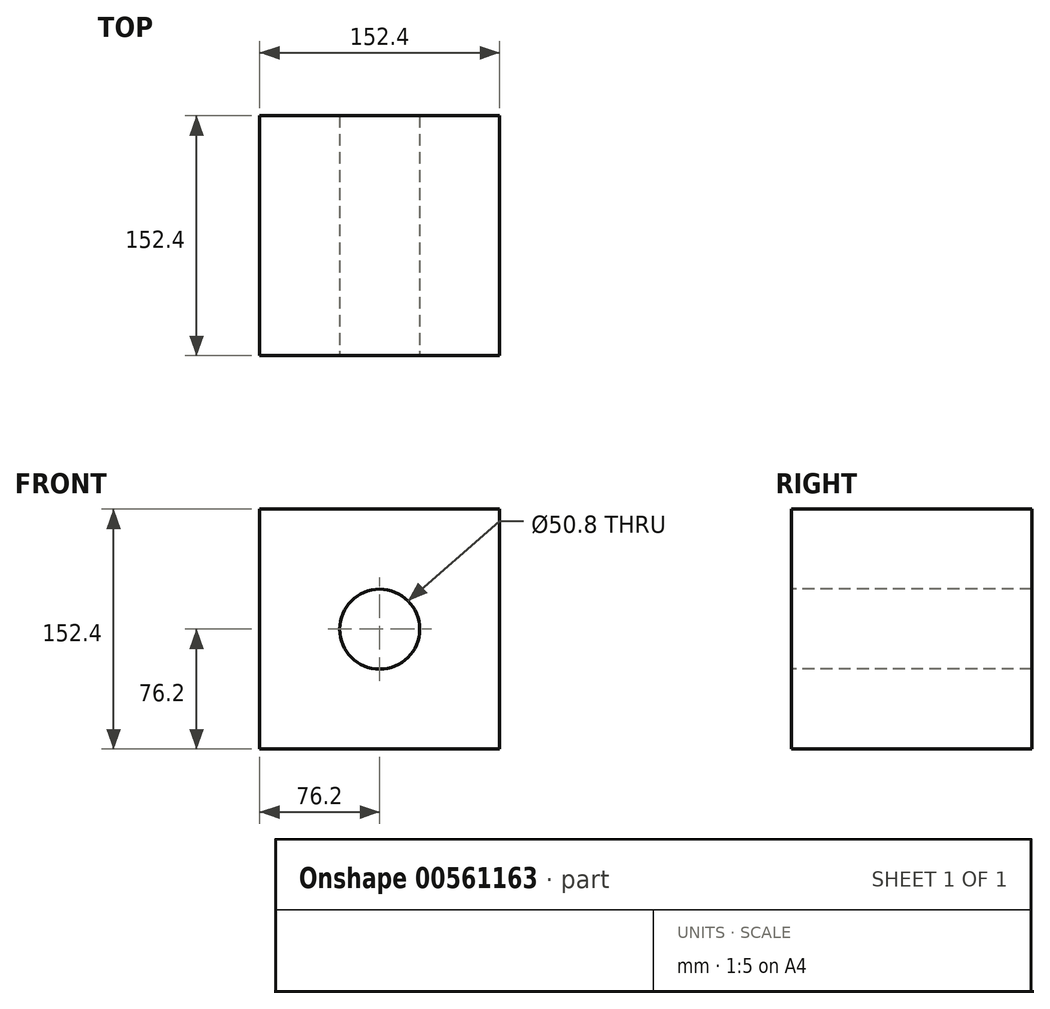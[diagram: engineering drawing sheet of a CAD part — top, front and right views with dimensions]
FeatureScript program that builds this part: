
annotation { "Feature Type Name" : "Feature", "Feature Type Description" : "" }
export const myFeature = defineFeature(function(context is Context, id is Id, definition is map)
    precondition{}
    {
        {
            var Q0;
            Q0=qCreatedBy(makeId("Top.planeOp"),FACE);
            var sketch = newSketch(context, id + "F0", { "sketchPlane" : qUnion([Q0])});
            skLineSegment(sketch, "E0.bottom", {"start": v(-76.2, 76.2) * mm, "end": v(76.2, 76.2) * mm});
            skLineSegment(sketch, "E0.top", {"start": v(-76.2, -76.2) * mm, "end": v(76.2, -76.2) * mm});
            skLineSegment(sketch, "E0.left", {"start": v(-76.2, 76.2) * mm, "end": v(-76.2, -76.2) * mm});
            skLineSegment(sketch, "E0.right", {"start": v(76.2, 76.2) * mm, "end": v(76.2, -76.2) * mm});
            skPoint(sketch, "E0.middle", {"position": v(0, 0) * mm});
            skSolve(sketch);
        }
        {
            var Q0;
            Q0 = qSketchRegion(id + "F0", true);
            extrude(context, id + "F1", {"entities" : qUnion([Q0]), "depth" : 152.4 * mm, "offsetDistance" : 25.4 * mm});
        }
        {
            var Q0;
            Q0=makeQuery(id+"F1.opExtrude","SWEPT_FACE",FACE,{"disambiguationData":[OSD([sQuery(id+"F0.wireOp",EDGE,"E0.top")])]});
            var sketch = newSketch(context, id + "F2", { "sketchPlane" : qUnion([Q0])});
            skCircle(sketch, "E1", {"center": v(0, 76.2) * mm, "radius": 25.4 * mm});
            skPoint(sketch, "E1.centerSnap0", {"position": v(76.2, 76.2) * mm});
            skSolve(sketch);
        }
        {
            var Q0;
            Q0 = qSketchRegion(id + "F2", true);
            extrude(context, id + "F3", {"entities" : qUnion([Q0]), "operationType" : NewBodyOperationType.REMOVE, "oppositeDirection" : true, "depth" : 152.4 * mm, "offsetDistance" : 25.4 * mm});
        }
    });
